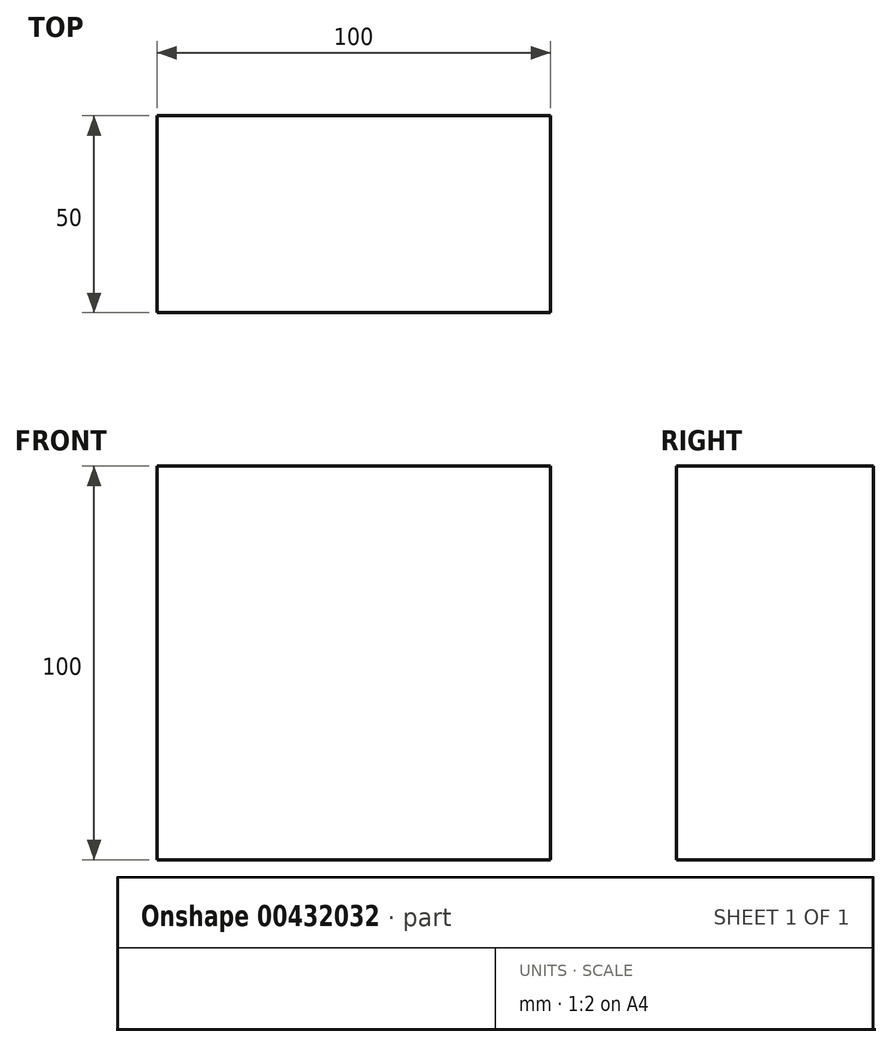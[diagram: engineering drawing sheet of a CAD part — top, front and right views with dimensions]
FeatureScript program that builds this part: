
annotation { "Feature Type Name" : "Feature", "Feature Type Description" : "" }
export const myFeature = defineFeature(function(context is Context, id is Id, definition is map)
    precondition{}
    {
        {
            var Q0;
            Q0=qCreatedBy(makeId("Front.planeOp"),FACE);
            var sketch = newSketch(context, id + "F0", { "sketchPlane" : qUnion([Q0])});
            skLineSegment(sketch, "E0", {"start": v(0, 0) * mm, "end": v(100, 0) * mm});
            skLineSegment(sketch, "E1", {"start": v(100, 0) * mm, "end": v(100, 100) * mm});
            skLineSegment(sketch, "E2", {"start": v(100, 100) * mm, "end": v(0, 100) * mm});
            skLineSegment(sketch, "E3", {"start": v(0, 100) * mm, "end": v(0, 0) * mm});
            skSolve(sketch);
        }
        {
            var Q0;
            Q0=makeQuery(id+"F0.imprint","IMPRINT",FACE,{"disambiguationData":[TD([[makeQuery(id+"F0.imprint","IMPRINT",EDGE,{"derivedFrom":sQuery(id+"F0.wireOp",EDGE,"E0")}),1.0]])]});
            extrude(context, id + "F1", {"entities" : qUnion([Q0]), "depth" : 50 * mm});
        }
    });
